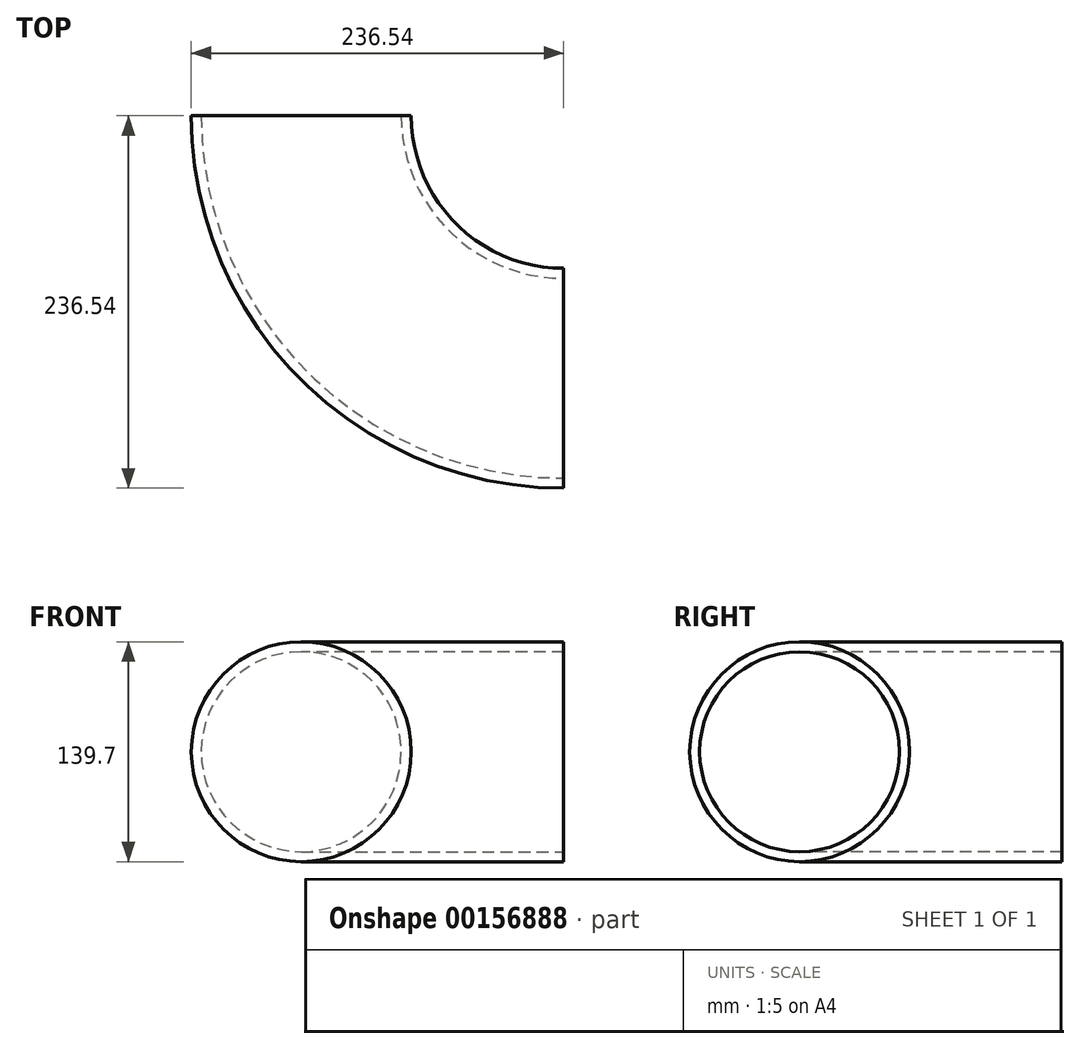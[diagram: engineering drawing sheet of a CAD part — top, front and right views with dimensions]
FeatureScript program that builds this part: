
annotation { "Feature Type Name" : "Feature", "Feature Type Description" : "" }
export const myFeature = defineFeature(function(context is Context, id is Id, definition is map)
    precondition{}
    {
        {
            var Q0;
            Q0=qCreatedBy(makeId("Right.planeOp"),FACE);
            var sketch = newSketch(context, id + "F0", { "sketchPlane" : qUnion([Q0])});
            skCircle(sketch, "E0", {"center": v(0, 0) * mm, "radius": 69.85 * mm});
            skCircle(sketch, "E1", {"center": v(0, 0) * mm, "radius": 63.5 * mm});
            skLineSegment(sketch, "E2", {"start": v(166.69, 96.97) * mm, "end": v(166.69, -105.26) * mm});
            skSolve(sketch);
        }
        {
            var Q0;
            Q0=makeQuery(id+"F0.imprint","IMPRINT",FACE,{"disambiguationData":[TD([[makeQuery(id+"F0.imprint","IMPRINT",EDGE,{"derivedFrom":sQuery(id+"F0.wireOp",EDGE,"E0")}),1.0]])]});
            var Q1;
            Q1=sQuery(id+"F0.wireOp",EDGE,"E2");
            revolve(context, id + "F1", {"entities" : qUnion([Q0]), "axis" : qUnion([Q1]), "revolveType" : RevolveType.ONE_DIRECTION, "angle" : 90 * degree});
        }
    });
